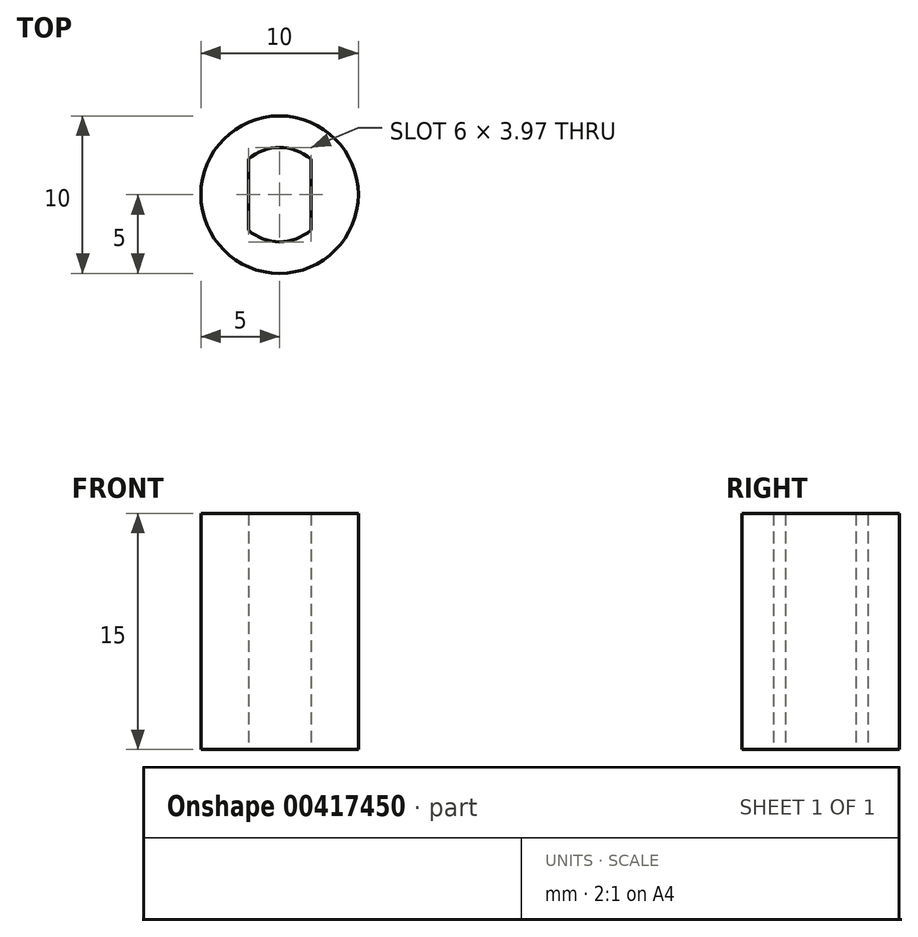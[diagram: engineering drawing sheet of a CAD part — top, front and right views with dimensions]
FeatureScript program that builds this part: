
annotation { "Feature Type Name" : "Feature", "Feature Type Description" : "" }
export const myFeature = defineFeature(function(context is Context, id is Id, definition is map)
    precondition{}
    {
        {
            var Q0;
            Q0=qCreatedBy(makeId("Top.planeOp"),FACE);
            var sketch = newSketch(context, id + "F0", { "sketchPlane" : qUnion([Q0])});
            skCircle(sketch, "E0", {"center": v(0, 0) * mm, "radius": 5 * mm});
            skCircle(sketch, "E1", {"center": v(0, 0) * mm, "radius": 3 * mm});
            skLineSegment(sketch, "E2", {"start": v(1.98, -2.25) * mm, "end": v(1.98, 2.25) * mm});
            skLineSegment(sketch, "E3.MirrorCS", {"start": v(-1.98, -2.25) * mm, "end": v(-1.98, 2.25) * mm});
            skSolve(sketch);
        }
        {
            var Q0;
            Q0=makeQuery(id+"F0.imprint","IMPRINT",FACE,{"disambiguationData":[TD([[makeQuery(id+"F0.imprint","IMPRINT",EDGE,{"derivedFrom":sQuery(id+"F0.wireOp",EDGE,"E0")}),1.0]])]});
            var Q1;
            {var subQ0=sQuery(id+"F0.wireOp",EDGE,"E3.MirrorCS");Q1=makeQuery(id+"F0.imprint","IMPRINT",FACE,{"disambiguationData":[TD([[makeQuery(id+"F0.imprint","IMPRINT",EDGE,{"derivedFrom":subQ0}),1.0]])]});}
            var Q2;
            {var subQ0=sQuery(id+"F0.wireOp",EDGE,"E2");Q2=makeQuery(id+"F0.imprint","IMPRINT",FACE,{"disambiguationData":[TD([[makeQuery(id+"F0.imprint","IMPRINT",EDGE,{"derivedFrom":subQ0}),-1.0]])]});}
            extrude(context, id + "F1", {"entities" : qUnion([Q0, Q1, Q2]), "depth" : 15 * mm});
        }
    });
